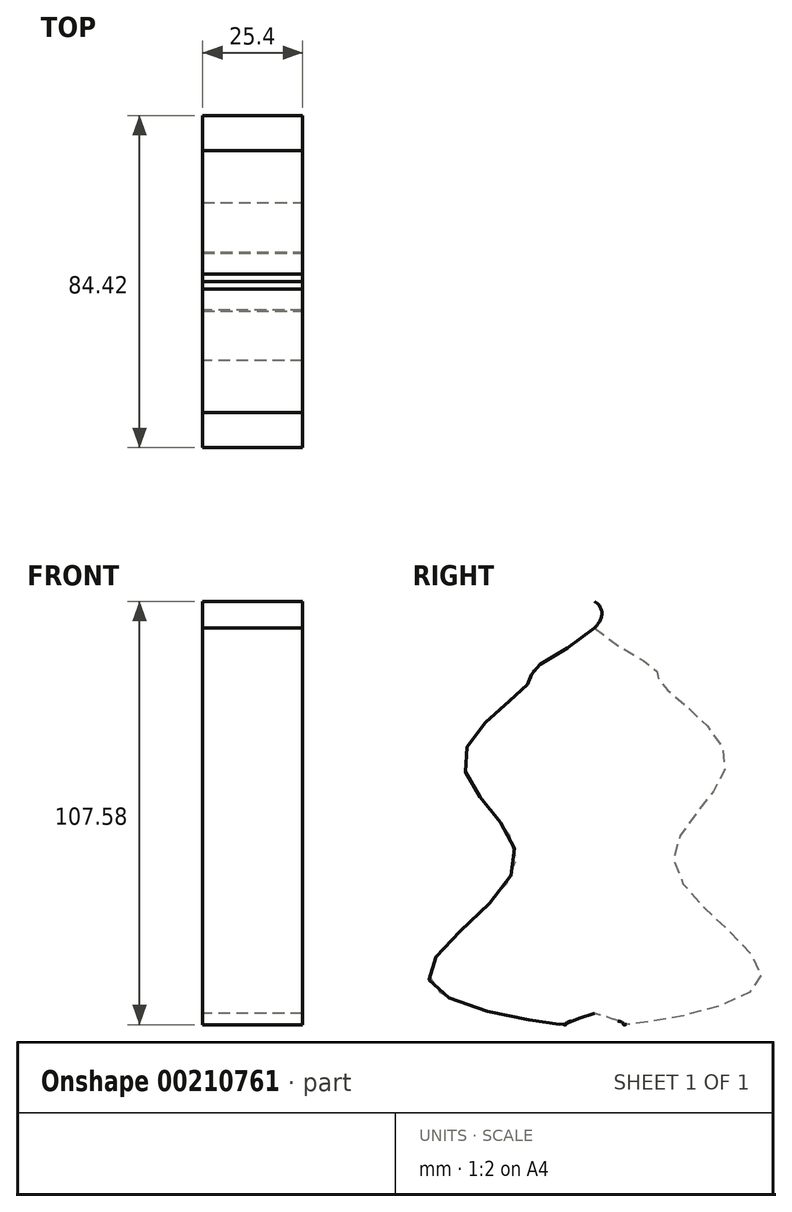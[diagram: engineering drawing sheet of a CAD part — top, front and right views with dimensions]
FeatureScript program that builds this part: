
annotation { "Feature Type Name" : "Feature", "Feature Type Description" : "" }
export const myFeature = defineFeature(function(context is Context, id is Id, definition is map)
    precondition{}
    {
        {
            var Q0;
            Q0=qCreatedBy(makeId("Right.planeOp"),FACE);
            var sketch = newSketch(context, id + "F0", { "sketchPlane" : qUnion([Q0])});
            skFitSpline(sketch, "E0", {"points": [v(0, 53.18) * mm, v(15.13, 36.23) * mm, v(16.35, 33) * mm, v(33.3, 12.82) * mm, v(20.18, -13.62) * mm, v(41.77, -43.69) * mm, v(7.26, -54.38) * mm, v(7.47, -54.18) * mm, v(0, -51.56) * mm], "startDerivative": vector(-161.09, -123.16) * mm, "endDerivative": vector(18.1, -3.7) * mm});
            skFitSpline(sketch, "E1.MirrorCS", {"points": [v(0, 53.18) * mm, v(-15.13, 36.23) * mm, v(-16.35, 33) * mm, v(-33.3, 12.82) * mm, v(-20.18, -13.62) * mm, v(-41.77, -43.69) * mm, v(-7.26, -54.38) * mm, v(-7.47, -54.18) * mm, v(0, -51.56) * mm], "startDerivative": vector(161.09, -123.16) * mm, "endDerivative": vector(-18.1, -3.7) * mm});
            skSolve(sketch);
        }
        {
            var Q0;
            Q0 = qSketchRegion(id + "F0", true);
            extrude(context, id + "F1", {"entities" : qUnion([Q0]), "depth" : 25.4 * mm});
        }
    });
